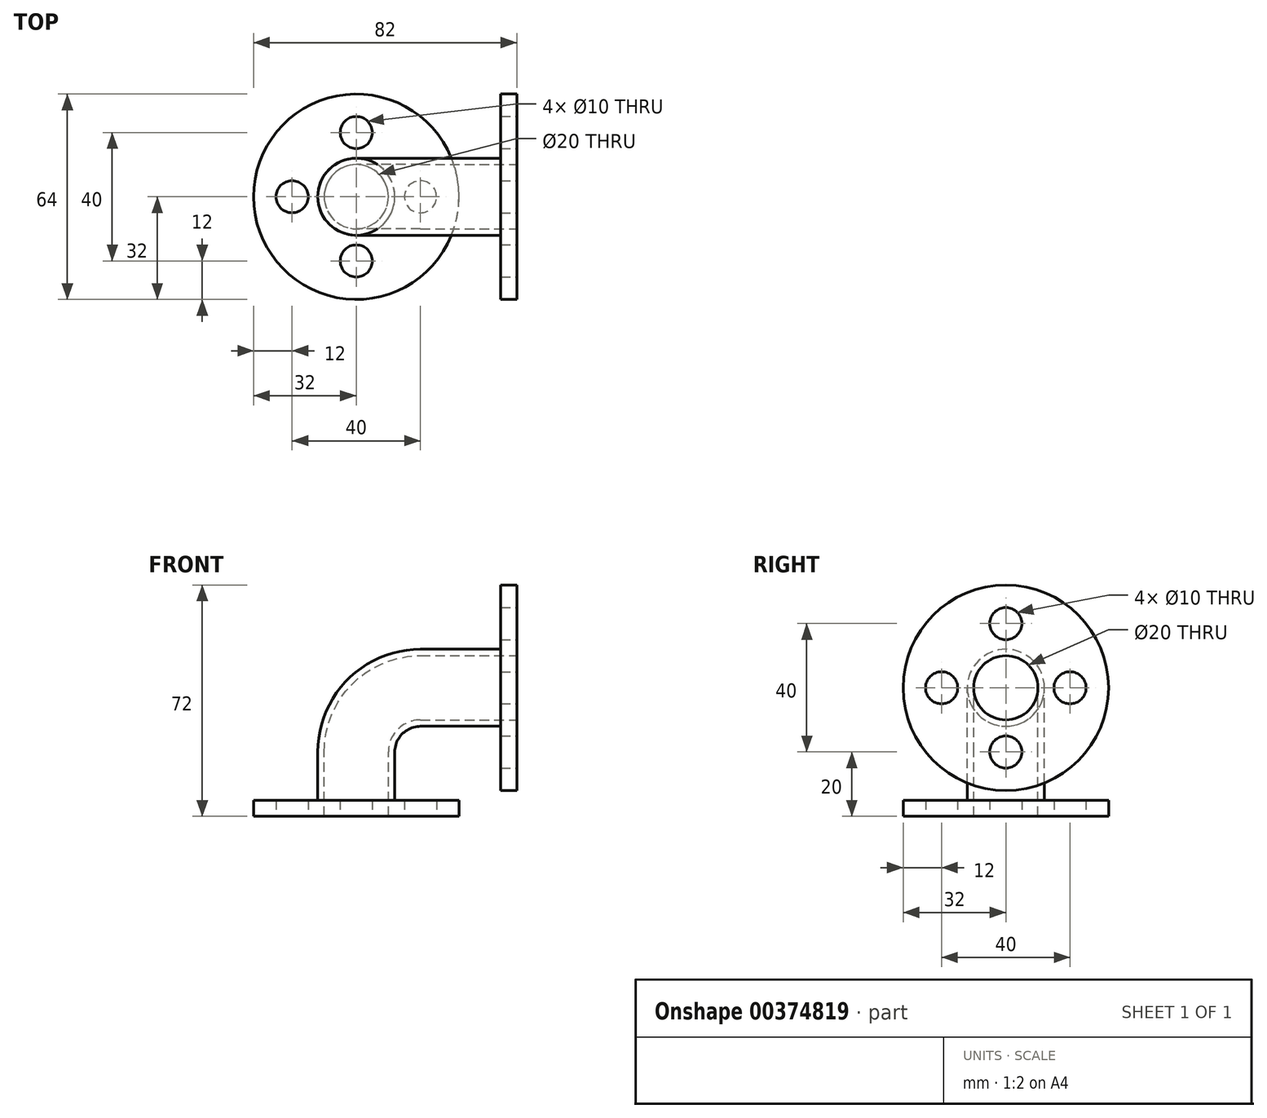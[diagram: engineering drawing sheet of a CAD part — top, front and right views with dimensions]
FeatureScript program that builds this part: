
annotation { "Feature Type Name" : "Feature", "Feature Type Description" : "" }
export const myFeature = defineFeature(function(context is Context, id is Id, definition is map)
    precondition{}
    {
        {
            var Q0;
            Q0=qCreatedBy(makeId("Front.planeOp"),FACE);
            var sketch = newSketch(context, id + "F0", { "sketchPlane" : qUnion([Q0])});
            skLineSegment(sketch, "E0", {"start": v(0, 0) * mm, "end": v(0, 20) * mm});
            skLineSegment(sketch, "E1", {"start": v(20, 40) * mm, "end": v(50, 40) * mm});
            skPoint(sketch, "E2.visualSharp", {"position": v(0, 40) * mm});
            skArc(sketch, "E2.filletArc", {"start": v(20, 40) * mm, "mid": v(5.86, 34.14) * mm, "end": v(0, 20) * mm});
            skSolve(sketch);
        }
        {
            var Q0;
            Q0=qCreatedBy(makeId("Top.planeOp"),FACE);
            var sketch = newSketch(context, id + "F1", { "sketchPlane" : qUnion([Q0])});
            skCircle(sketch, "E3", {"center": v(0, 0) * mm, "radius": 12 * mm});
            skSolve(sketch);
        }
        {
            var Q0;
            Q0=makeQuery(id+"F1.imprint","IMPRINT",FACE,{"disambiguationData":[TD([[makeQuery(id+"F1.imprint","IMPRINT",EDGE,{"derivedFrom":sQuery(id+"F1.wireOp",EDGE,"E3")}),1.0]])]});
            var Q1;
            Q1=sQuery(id+"F0.wireOp",EDGE,"E0");
            var Q2;
            Q2=sQuery(id+"F0.wireOp",EDGE,"E2.filletArc");
            var Q3;
            Q3=sQuery(id+"F0.wireOp",EDGE,"E1");
            sweep(context, id + "F2", {"profiles" : qUnion([Q0]), "path" : qUnion([Q1, Q2, Q3])});
        }
        {
            var Q0;
            Q0=makeQuery(id+"F2.opSweep","CAP_FACE",FACE,{"disambiguationData":[OSD([sQuery(id+"F0.wireOp",VERTEX,"E0.start"),sQuery(id+"F1.wireOp",EDGE,"E3")])],"isStart":true});
            var sketch = newSketch(context, id + "F3", { "sketchPlane" : qUnion([Q0])});
            skCircle(sketch, "E4", {"center": v(0, 0) * mm, "radius": 10 * mm});
            skSolve(sketch);
        }
        {
            var Q0;
            Q0=makeQuery(id+"F3.imprint","IMPRINT",FACE,{"disambiguationData":[TD([[makeQuery(id+"F3.imprint","IMPRINT",EDGE,{"derivedFrom":sQuery(id+"F3.wireOp",EDGE,"E4")}),1.0]])]});
            var Q1;
            Q1=qConstructionFilter(qBodyType(qCreatedBy(id+"F0",EDGE),BodyType.WIRE),ConstructionObject.NO);
            sweep(context, id + "F4", {"operationType" : NewBodyOperationType.REMOVE, "profiles" : qUnion([Q0]), "path" : qUnion([Q1])});
        }
        {
            var Q0;
            Q0=makeQuery(id+"F2.opSweep","CAP_FACE",FACE,{"disambiguationData":[OSD([sQuery(id+"F0.wireOp",VERTEX,"E1.end"),sQuery(id+"F1.wireOp",EDGE,"E3")])],"isStart":false});
            var sketch = newSketch(context, id + "F5", { "sketchPlane" : qUnion([Q0])});
            skCircle(sketch, "E5", {"center": v(0, 40) * mm, "radius": 32 * mm});
            skSolve(sketch);
        }
        {
            var Q0;
            Q0=makeQuery(id+"F5.imprint","IMPRINT",FACE,{"disambiguationData":[TD([[makeQuery(id+"F5.imprint","IMPRINT",EDGE,{"derivedFrom":sQuery(id+"F5.wireOp",EDGE,"E5")}),1.0]])]});
            extrude(context, id + "F6", {"entities" : qUnion([Q0]), "operationType" : NewBodyOperationType.ADD, "oppositeDirection" : true, "depth" : 5 * mm});
        }
        {
            var Q0;
            Q0=makeQuery(id+"F2.opSweep","CAP_FACE",FACE,{"disambiguationData":[OSD([sQuery(id+"F0.wireOp",VERTEX,"E0.start"),sQuery(id+"F1.wireOp",EDGE,"E3")])],"isStart":true});
            var sketch = newSketch(context, id + "F7", { "sketchPlane" : qUnion([Q0])});
            skCircle(sketch, "E6", {"center": v(0, 0) * mm, "radius": 32 * mm});
            skSolve(sketch);
        }
        {
            var Q0;
            Q0=makeQuery(id+"F7.imprint","IMPRINT",FACE,{"disambiguationData":[TD([[makeQuery(id+"F7.imprint","IMPRINT",EDGE,{"derivedFrom":sQuery(id+"F7.wireOp",EDGE,"E6")}),1.0]])]});
            extrude(context, id + "F8", {"entities" : qUnion([Q0]), "operationType" : NewBodyOperationType.ADD, "oppositeDirection" : true, "depth" : 5 * mm});
        }
        {
            var Q0;
            {var subQ0=sQuery(id+"F1.wireOp",EDGE,"E3");var subQ1=sQuery(id+"F0.wireOp",VERTEX,"E1.end");Q0=makeQuery(id+"F6.boolean.opBoolean","MERGE",FACE,{"derivedFrom":[makeQuery(id+"F2.opSweep","CAP_FACE",FACE,{"disambiguationData":[OSD([subQ1,subQ0])],"isStart":false}),makeQuery(id+"F6.opExtrude","CAP_FACE",FACE,{"disambiguationData":[OSD([subQ1,subQ0,sQuery(id+"F5.wireOp",EDGE,"E5")])],"isStart":true})]});}
            var sketch = newSketch(context, id + "F9", { "sketchPlane" : qUnion([Q0])});
            skCircle(sketch, "E7", {"center": v(0, 60) * mm, "radius": 5 * mm});
            skLineSegment(sketch, "E8", {"start": v(0, 40) * mm, "end": v(0, 60) * mm, "construction": true});
            skLineSegment(sketch, "E9", {"start": v(0, 40) * mm, "end": v(0, 20) * mm, "construction": true});
            skLineSegment(sketch, "E10", {"start": v(0, 40) * mm, "end": v(20, 40) * mm, "construction": true});
            skLineSegment(sketch, "E11", {"start": v(0, 40) * mm, "end": v(-20, 40) * mm, "construction": true});
            skCircle(sketch, "E12", {"center": v(20, 40) * mm, "radius": 5 * mm});
            skCircle(sketch, "E13", {"center": v(0, 20) * mm, "radius": 5 * mm});
            skCircle(sketch, "E14", {"center": v(-20, 40) * mm, "radius": 5 * mm});
            skSolve(sketch);
        }
        {
            var Q0;
            Q0=makeQuery(id+"F9.imprint","IMPRINT",FACE,{"disambiguationData":[TD([[makeQuery(id+"F9.imprint","IMPRINT",EDGE,{"derivedFrom":sQuery(id+"F9.wireOp",EDGE,"E12")}),1.0]])]});
            var Q1;
            Q1=makeQuery(id+"F9.imprint","IMPRINT",FACE,{"disambiguationData":[TD([[makeQuery(id+"F9.imprint","IMPRINT",EDGE,{"derivedFrom":sQuery(id+"F9.wireOp",EDGE,"E7")}),1.0]])]});
            var Q2;
            Q2=makeQuery(id+"F9.imprint","IMPRINT",FACE,{"disambiguationData":[TD([[makeQuery(id+"F9.imprint","IMPRINT",EDGE,{"derivedFrom":sQuery(id+"F9.wireOp",EDGE,"E14")}),1.0]])]});
            var Q3;
            Q3=makeQuery(id+"F9.imprint","IMPRINT",FACE,{"disambiguationData":[TD([[makeQuery(id+"F9.imprint","IMPRINT",EDGE,{"derivedFrom":sQuery(id+"F9.wireOp",EDGE,"E13")}),1.0]])]});
            var Q4;
            Q4=makeQuery(id+"F6.opExtrude","CAP_FACE",FACE,{"disambiguationData":[OSD([sQuery(id+"F0.wireOp",VERTEX,"E1.end"),sQuery(id+"F1.wireOp",EDGE,"E3"),sQuery(id+"F5.wireOp",EDGE,"E5")])],"isStart":false});
            extrude(context, id + "F10", {"entities" : qUnion([Q0, Q1, Q2, Q3]), "operationType" : NewBodyOperationType.REMOVE, "endBound" : BoundingType.UP_TO_SURFACE, "oppositeDirection" : true, "endBoundEntityFace" : qUnion([Q4]), "depth" : 25 * mm});
        }
        {
            var Q0;
            {var subQ0=sQuery(id+"F1.wireOp",EDGE,"E3");var subQ1=sQuery(id+"F0.wireOp",VERTEX,"E0.start");Q0=makeQuery(id+"F8.boolean.opBoolean","MERGE",FACE,{"derivedFrom":[makeQuery(id+"F2.opSweep","CAP_FACE",FACE,{"disambiguationData":[OSD([subQ1,subQ0])],"isStart":true}),makeQuery(id+"F8.opExtrude","CAP_FACE",FACE,{"disambiguationData":[OSD([subQ1,subQ0,sQuery(id+"F7.wireOp",EDGE,"E6")])],"isStart":true})]});}
            var sketch = newSketch(context, id + "F11", { "sketchPlane" : qUnion([Q0])});
            skCircle(sketch, "E15", {"center": v(0, 20) * mm, "radius": 5 * mm});
            skCircle(sketch, "E16.1.0", {"center": v(-20, 0) * mm, "radius": 5 * mm});
            skCircle(sketch, "E16.2.0", {"center": v(0, -20) * mm, "radius": 5 * mm});
            skPoint(sketch, "E16.center", {"position": v(0, 0) * mm});
            skCircle(sketch, "E17.1.3.0", {"center": v(20, 0) * mm, "radius": 5 * mm});
            skSolve(sketch);
        }
        {
            var Q0;
            Q0=makeQuery(id+"F11.imprint","IMPRINT",FACE,{"disambiguationData":[TD([[makeQuery(id+"F11.imprint","IMPRINT",EDGE,{"derivedFrom":sQuery(id+"F11.wireOp",EDGE,"E17.1.3.0")}),1.0]])]});
            var Q1;
            Q1=makeQuery(id+"F11.imprint","IMPRINT",FACE,{"disambiguationData":[TD([[makeQuery(id+"F11.imprint","IMPRINT",EDGE,{"derivedFrom":sQuery(id+"F11.wireOp",EDGE,"E16.2.0")}),1.0]])]});
            var Q2;
            Q2=makeQuery(id+"F11.imprint","IMPRINT",FACE,{"disambiguationData":[TD([[makeQuery(id+"F11.imprint","IMPRINT",EDGE,{"derivedFrom":sQuery(id+"F11.wireOp",EDGE,"E16.1.0")}),1.0]])]});
            var Q3;
            Q3=makeQuery(id+"F11.imprint","IMPRINT",FACE,{"disambiguationData":[TD([[makeQuery(id+"F11.imprint","IMPRINT",EDGE,{"derivedFrom":sQuery(id+"F11.wireOp",EDGE,"E15")}),1.0]])]});
            var Q4;
            Q4=makeQuery(id+"F8.opExtrude","CAP_FACE",FACE,{"disambiguationData":[OSD([sQuery(id+"F0.wireOp",VERTEX,"E0.start"),sQuery(id+"F1.wireOp",EDGE,"E3"),sQuery(id+"F7.wireOp",EDGE,"E6")])],"isStart":false});
            extrude(context, id + "F12", {"entities" : qUnion([Q0, Q1, Q2, Q3]), "operationType" : NewBodyOperationType.REMOVE, "endBound" : BoundingType.UP_TO_SURFACE, "oppositeDirection" : true, "endBoundEntityFace" : qUnion([Q4]), "depth" : 25 * mm});
        }
    });
